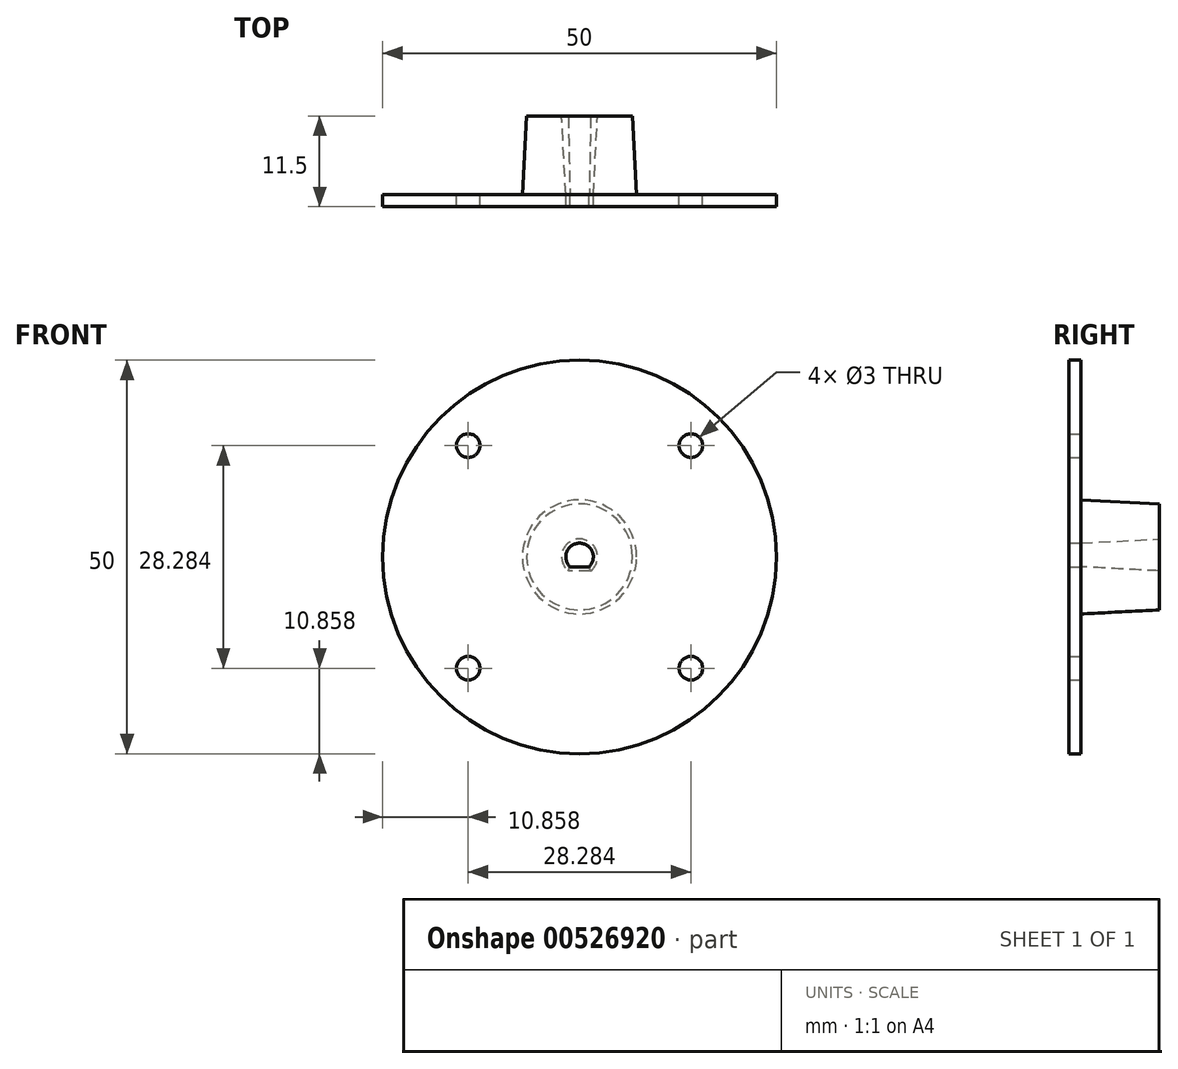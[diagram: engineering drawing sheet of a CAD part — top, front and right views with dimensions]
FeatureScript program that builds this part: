
annotation { "Feature Type Name" : "Feature", "Feature Type Description" : "" }
export const myFeature = defineFeature(function(context is Context, id is Id, definition is map)
    precondition{}
    {
        {
            var Q0;
            Q0=qCreatedBy(makeId("Front.planeOp"),FACE);
            var sketch = newSketch(context, id + "F0", { "sketchPlane" : qUnion([Q0])});
            skCircle(sketch, "E0", {"center": v(0, 0) * mm, "radius": 60 * mm, "construction": true});
            skCircle(sketch, "E1", {"center": v(0, 0) * mm, "radius": 7.25 * mm});
            skArc(sketch, "E2", {"start": v(-1.22, -1.25) * mm, "mid": v(0, 1.75) * mm, "end": v(1.22, -1.25) * mm});
            skLineSegment(sketch, "E3", {"start": v(-1.22, -1.25) * mm, "end": v(1.22, -1.25) * mm});
            skCircle(sketch, "E4", {"center": v(0, 0) * mm, "radius": 25 * mm});
            skCircle(sketch, "E5", {"center": v(-14.14, -14.14) * mm, "radius": 1.5 * mm});
            skLineSegment(sketch, "E6", {"start": v(-14.14, -14.14) * mm, "end": v(0, 0) * mm, "construction": true});
            skLineSegment(sketch, "E7", {"start": v(0, 0) * mm, "end": v(0, -6.48) * mm, "construction": true});
            skCircle(sketch, "E8.1.0", {"center": v(14.14, -14.14) * mm, "radius": 1.5 * mm});
            skCircle(sketch, "E8.2.0", {"center": v(14.14, 14.14) * mm, "radius": 1.5 * mm});
            skCircle(sketch, "E8.3.0", {"center": v(-14.14, 14.14) * mm, "radius": 1.5 * mm});
            skSolve(sketch);
        }
        {
            var Q0;
            Q0=makeQuery(id+"F0.imprint","IMPRINT",FACE,{"disambiguationData":[TD([[makeQuery(id+"F0.imprint","IMPRINT",EDGE,{"derivedFrom":sQuery(id+"F0.wireOp",EDGE,"E1")}),1.0]])]});
            extrude(context, id + "F1", {"entities" : qUnion([Q0]), "oppositeDirection" : true, "depth" : 10 * mm, "offsetDistance" : 25 * mm, "hasDraft" : true, "draftAngle" : 3 * degree, "draftPullDirection" : true});
        }
        {
            var Q0;
            Q0=makeQuery(id+"F0.imprint","IMPRINT",FACE,{"disambiguationData":[TD([[makeQuery(id+"F0.imprint","IMPRINT",EDGE,{"derivedFrom":sQuery(id+"F0.wireOp",EDGE,"E1")}),-1.0]])]});
            var Q1;
            Q1=makeQuery(id+"F0.imprint","IMPRINT",FACE,{"disambiguationData":[TD([[makeQuery(id+"F0.imprint","IMPRINT",EDGE,{"derivedFrom":sQuery(id+"F0.wireOp",EDGE,"E1")}),1.0]])]});
            extrude(context, id + "F2", {"entities" : qUnion([Q0, Q1]), "operationType" : NewBodyOperationType.ADD, "depth" : 1.5 * mm, "offsetDistance" : 25 * mm});
        }
    });
